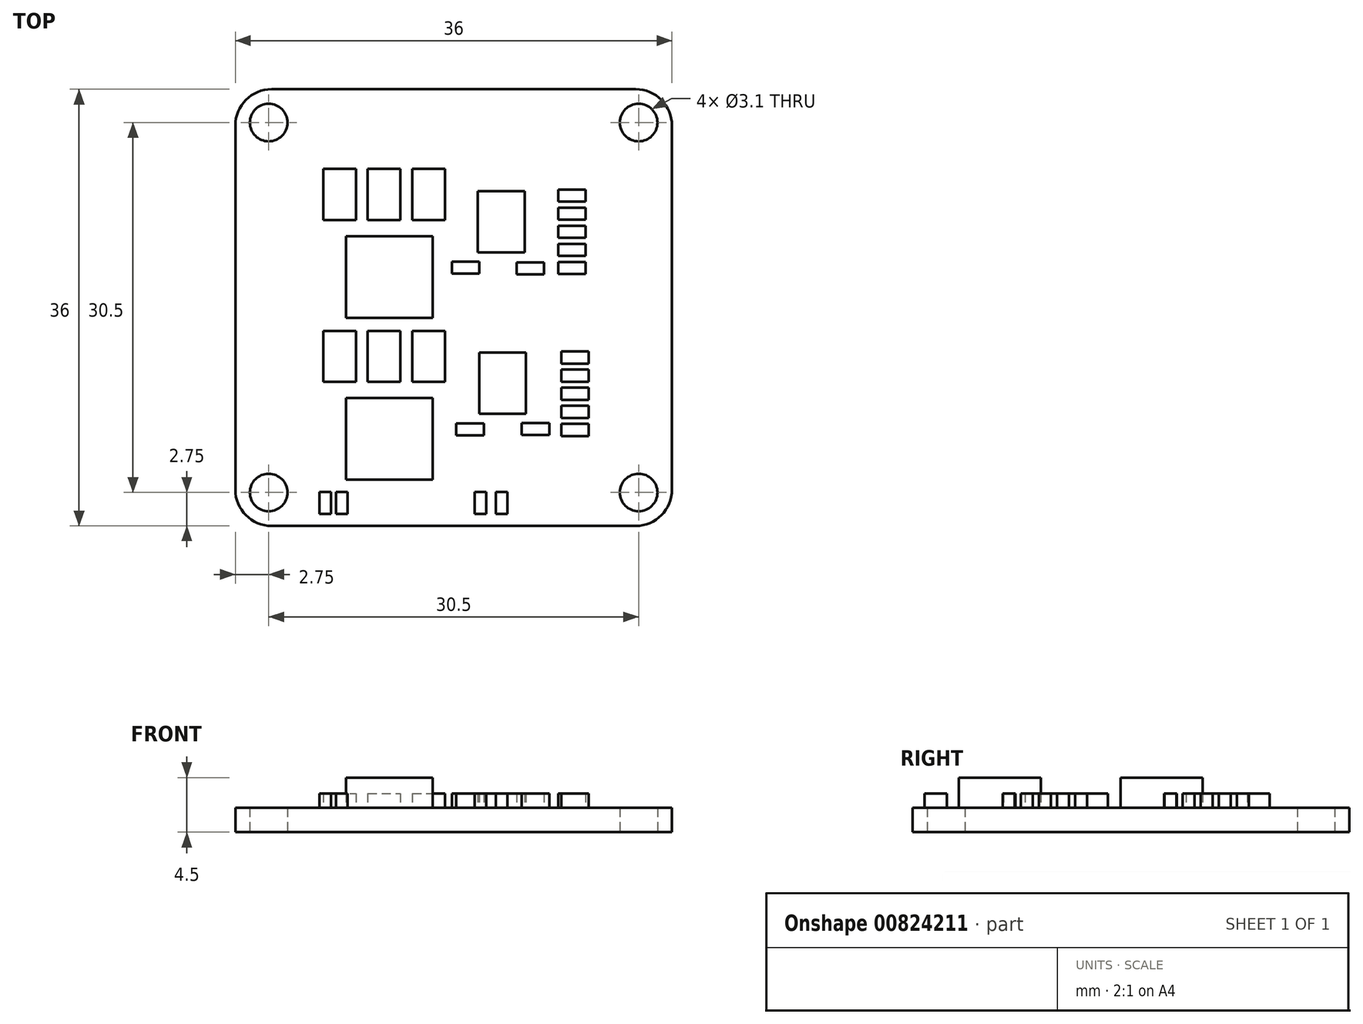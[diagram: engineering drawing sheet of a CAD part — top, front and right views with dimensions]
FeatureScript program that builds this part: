
annotation { "Feature Type Name" : "Feature", "Feature Type Description" : "" }
export const myFeature = defineFeature(function(context is Context, id is Id, definition is map)
    precondition{}
    {
        {
            var Q0;
            Q0=qCreatedBy(makeId("Top.planeOp"),FACE);
            var sketch = newSketch(context, id + "F0", { "sketchPlane" : qUnion([Q0])});
            skLineSegment(sketch, "E0", {"start": v(18, 17.73) * mm, "end": v(-18, -17.73) * mm, "construction": true});
            skLineSegment(sketch, "E1.bottom", {"start": v(18, -18) * mm, "end": v(-18, -18) * mm});
            skLineSegment(sketch, "E1.top", {"start": v(18, 18) * mm, "end": v(-18, 18) * mm});
            skLineSegment(sketch, "E1.left", {"start": v(18, -18) * mm, "end": v(18, 18) * mm});
            skLineSegment(sketch, "E1.right", {"start": v(-18, -18) * mm, "end": v(-18, 18) * mm});
            skPoint(sketch, "E1.middle", {"position": v(0, 0) * mm});
            skLineSegment(sketch, "E2.bottom", {"start": v(15.25, -15.25) * mm, "end": v(-15.25, -15.25) * mm, "construction": true});
            skLineSegment(sketch, "E2.top", {"start": v(15.25, 15.25) * mm, "end": v(-15.25, 15.25) * mm, "construction": true});
            skLineSegment(sketch, "E2.left", {"start": v(15.25, -15.25) * mm, "end": v(15.25, 15.25) * mm, "construction": true});
            skLineSegment(sketch, "E2.right", {"start": v(-15.25, -15.25) * mm, "end": v(-15.25, 15.25) * mm, "construction": true});
            skCircle(sketch, "E3", {"center": v(-15.25, 15.25) * mm, "radius": 1.55 * mm});
            skCircle(sketch, "E4", {"center": v(15.25, 15.25) * mm, "radius": 1.55 * mm});
            skCircle(sketch, "E5", {"center": v(-15.25, -15.25) * mm, "radius": 1.55 * mm});
            skCircle(sketch, "E6", {"center": v(15.25, -15.25) * mm, "radius": 1.55 * mm});
            skSolve(sketch);
        }
        {
            var Q0;
            Q0 = qSketchRegion(id + "F0", true);
            extrude(context, id + "F1", {"entities" : qUnion([Q0]), "depth" : 2 * mm, "offsetDistance" : 25 * mm});
        }
        {
            var Q0;
            Q0=makeQuery(id+"F1.opExtrude","CAP_FACE",FACE,{"disambiguationData":[OSD([sQuery(id+"F0.wireOp",EDGE,"E1.bottom"),sQuery(id+"F0.wireOp",EDGE,"E1.top"),sQuery(id+"F0.wireOp",EDGE,"E1.left"),sQuery(id+"F0.wireOp",EDGE,"E1.right"),sQuery(id+"F0.wireOp",EDGE,"E3"),sQuery(id+"F0.wireOp",EDGE,"E4"),sQuery(id+"F0.wireOp",EDGE,"E5"),sQuery(id+"F0.wireOp",EDGE,"E6")])],"isStart":false});
            var sketch = newSketch(context, id + "F2", { "sketchPlane" : qUnion([Q0])});
            skLineSegment(sketch, "E7.bottom", {"start": v(-10.76, 11.42) * mm, "end": v(-8.06, 11.42) * mm});
            skLineSegment(sketch, "E7.top", {"start": v(-10.76, 7.22) * mm, "end": v(-8.06, 7.22) * mm});
            skLineSegment(sketch, "E7.left", {"start": v(-10.76, 11.42) * mm, "end": v(-10.76, 7.22) * mm});
            skLineSegment(sketch, "E7.right", {"start": v(-8.06, 11.42) * mm, "end": v(-8.06, 7.22) * mm});
            skLineSegment(sketch, "E8.0.1.0", {"start": v(-10.76, -1.92) * mm, "end": v(-8.06, -1.92) * mm});
            skLineSegment(sketch, "E8.0.1.1", {"start": v(-10.76, -1.92) * mm, "end": v(-10.76, -6.12) * mm});
            skLineSegment(sketch, "E8.0.1.2", {"start": v(-8.06, -1.92) * mm, "end": v(-8.06, -6.12) * mm});
            skLineSegment(sketch, "E8.0.1.3", {"start": v(-10.76, -6.12) * mm, "end": v(-8.06, -6.12) * mm});
            skLineSegment(sketch, "E8.1.0.0", {"start": v(-7.08, 11.42) * mm, "end": v(-4.38, 11.42) * mm});
            skLineSegment(sketch, "E8.1.0.1", {"start": v(-7.08, 11.42) * mm, "end": v(-7.08, 7.22) * mm});
            skLineSegment(sketch, "E8.1.0.2", {"start": v(-4.38, 11.42) * mm, "end": v(-4.38, 7.22) * mm});
            skLineSegment(sketch, "E8.1.0.3", {"start": v(-7.08, 7.22) * mm, "end": v(-4.38, 7.22) * mm});
            skLineSegment(sketch, "E8.1.1.0", {"start": v(-7.08, -1.92) * mm, "end": v(-4.38, -1.92) * mm});
            skLineSegment(sketch, "E8.1.1.1", {"start": v(-7.08, -1.92) * mm, "end": v(-7.08, -6.12) * mm});
            skLineSegment(sketch, "E8.1.1.2", {"start": v(-4.38, -1.92) * mm, "end": v(-4.38, -6.12) * mm});
            skLineSegment(sketch, "E8.1.1.3", {"start": v(-7.08, -6.12) * mm, "end": v(-4.38, -6.12) * mm});
            skLineSegment(sketch, "E8.2.0.0", {"start": v(-3.41, 11.42) * mm, "end": v(-0.71, 11.42) * mm});
            skLineSegment(sketch, "E8.2.0.1", {"start": v(-3.41, 11.42) * mm, "end": v(-3.41, 7.22) * mm});
            skLineSegment(sketch, "E8.2.0.2", {"start": v(-0.71, 11.42) * mm, "end": v(-0.71, 7.22) * mm});
            skLineSegment(sketch, "E8.2.0.3", {"start": v(-3.41, 7.22) * mm, "end": v(-0.71, 7.22) * mm});
            skLineSegment(sketch, "E8.2.1.0", {"start": v(-3.41, -1.92) * mm, "end": v(-0.71, -1.92) * mm});
            skLineSegment(sketch, "E8.2.1.1", {"start": v(-3.41, -1.92) * mm, "end": v(-3.41, -6.12) * mm});
            skLineSegment(sketch, "E8.2.1.2", {"start": v(-0.71, -1.92) * mm, "end": v(-0.71, -6.12) * mm});
            skLineSegment(sketch, "E8.2.1.3", {"start": v(-3.41, -6.12) * mm, "end": v(-0.71, -6.12) * mm});
            skLineSegment(sketch, "E8.direction1", {"start": v(-10.76, 7.22) * mm, "end": v(-7.08, 7.22) * mm, "construction": true});
            skLineSegment(sketch, "E8.direction2", {"start": v(-10.76, 7.22) * mm, "end": v(-10.76, -6.12) * mm, "construction": true});
            skLineSegment(sketch, "E9.bottom", {"start": v(1.98, 9.58) * mm, "end": v(5.84, 9.58) * mm});
            skLineSegment(sketch, "E9.top", {"start": v(1.98, 4.53) * mm, "end": v(5.84, 4.53) * mm});
            skLineSegment(sketch, "E9.left", {"start": v(1.98, 9.58) * mm, "end": v(1.98, 4.53) * mm});
            skLineSegment(sketch, "E9.right", {"start": v(5.84, 9.58) * mm, "end": v(5.84, 4.53) * mm});
            skLineSegment(sketch, "E10.bottom", {"start": v(2.1, -3.7) * mm, "end": v(5.97, -3.7) * mm});
            skLineSegment(sketch, "E10.top", {"start": v(2.1, -8.75) * mm, "end": v(5.97, -8.75) * mm});
            skLineSegment(sketch, "E10.left", {"start": v(2.1, -3.7) * mm, "end": v(2.1, -8.75) * mm});
            skLineSegment(sketch, "E10.right", {"start": v(5.97, -3.7) * mm, "end": v(5.97, -8.75) * mm});
            skLineSegment(sketch, "E11.bottom", {"start": v(8.62, 9.72) * mm, "end": v(10.88, 9.72) * mm});
            skLineSegment(sketch, "E11.top", {"start": v(8.62, 8.73) * mm, "end": v(10.88, 8.73) * mm});
            skLineSegment(sketch, "E11.left", {"start": v(8.62, 9.72) * mm, "end": v(8.62, 8.73) * mm});
            skLineSegment(sketch, "E11.right", {"start": v(10.88, 9.72) * mm, "end": v(10.88, 8.73) * mm});
            skLineSegment(sketch, "E12.1.0.0", {"start": v(10.88, 8.23) * mm, "end": v(10.88, 7.24) * mm});
            skLineSegment(sketch, "E12.1.0.1", {"start": v(8.62, 8.23) * mm, "end": v(8.62, 7.24) * mm});
            skLineSegment(sketch, "E12.1.0.2", {"start": v(8.62, 8.23) * mm, "end": v(10.88, 8.23) * mm});
            skLineSegment(sketch, "E12.1.0.3", {"start": v(8.62, 7.24) * mm, "end": v(10.88, 7.24) * mm});
            skLineSegment(sketch, "E12.2.0.0", {"start": v(10.88, 6.73) * mm, "end": v(10.88, 5.74) * mm});
            skLineSegment(sketch, "E12.2.0.1", {"start": v(8.62, 6.73) * mm, "end": v(8.62, 5.74) * mm});
            skLineSegment(sketch, "E12.2.0.2", {"start": v(8.62, 6.73) * mm, "end": v(10.88, 6.73) * mm});
            skLineSegment(sketch, "E12.2.0.3", {"start": v(8.62, 5.74) * mm, "end": v(10.88, 5.74) * mm});
            skLineSegment(sketch, "E12.3.0.0", {"start": v(10.88, 5.24) * mm, "end": v(10.88, 4.25) * mm});
            skLineSegment(sketch, "E12.3.0.1", {"start": v(8.62, 5.24) * mm, "end": v(8.62, 4.25) * mm});
            skLineSegment(sketch, "E12.3.0.2", {"start": v(8.62, 5.24) * mm, "end": v(10.88, 5.24) * mm});
            skLineSegment(sketch, "E12.3.0.3", {"start": v(8.62, 4.25) * mm, "end": v(10.88, 4.25) * mm});
            skLineSegment(sketch, "E12.4.0.0", {"start": v(10.88, 3.75) * mm, "end": v(10.88, 2.76) * mm});
            skLineSegment(sketch, "E12.4.0.1", {"start": v(8.62, 3.75) * mm, "end": v(8.62, 2.76) * mm});
            skLineSegment(sketch, "E12.4.0.2", {"start": v(8.62, 3.75) * mm, "end": v(10.88, 3.75) * mm});
            skLineSegment(sketch, "E12.4.0.3", {"start": v(8.62, 2.76) * mm, "end": v(10.88, 2.76) * mm});
            skLineSegment(sketch, "E12.direction1", {"start": v(8.62, 8.73) * mm, "end": v(8.62, 7.24) * mm, "construction": true});
            skLineSegment(sketch, "E13.bottom", {"start": v(8.86, -3.63) * mm, "end": v(11.13, -3.63) * mm});
            skLineSegment(sketch, "E13.top", {"start": v(8.86, -4.62) * mm, "end": v(11.13, -4.62) * mm});
            skLineSegment(sketch, "E13.left", {"start": v(8.86, -3.63) * mm, "end": v(8.86, -4.62) * mm});
            skLineSegment(sketch, "E13.right", {"start": v(11.13, -3.63) * mm, "end": v(11.13, -4.62) * mm});
            skLineSegment(sketch, "E14.1.0.0", {"start": v(11.13, -5.12) * mm, "end": v(11.13, -6.1) * mm});
            skLineSegment(sketch, "E14.1.0.1", {"start": v(8.86, -5.12) * mm, "end": v(8.86, -6.1) * mm});
            skLineSegment(sketch, "E14.1.0.2", {"start": v(8.86, -5.12) * mm, "end": v(11.13, -5.12) * mm});
            skLineSegment(sketch, "E14.1.0.3", {"start": v(8.86, -6.1) * mm, "end": v(11.13, -6.1) * mm});
            skLineSegment(sketch, "E14.2.0.0", {"start": v(11.13, -6.61) * mm, "end": v(11.13, -7.6) * mm});
            skLineSegment(sketch, "E14.2.0.1", {"start": v(8.86, -6.61) * mm, "end": v(8.86, -7.6) * mm});
            skLineSegment(sketch, "E14.2.0.2", {"start": v(8.86, -6.61) * mm, "end": v(11.13, -6.61) * mm});
            skLineSegment(sketch, "E14.2.0.3", {"start": v(8.86, -7.6) * mm, "end": v(11.13, -7.6) * mm});
            skLineSegment(sketch, "E14.3.0.0", {"start": v(11.13, -8.1) * mm, "end": v(11.13, -9.1) * mm});
            skLineSegment(sketch, "E14.3.0.1", {"start": v(8.86, -8.1) * mm, "end": v(8.86, -9.1) * mm});
            skLineSegment(sketch, "E14.3.0.2", {"start": v(8.86, -8.1) * mm, "end": v(11.13, -8.1) * mm});
            skLineSegment(sketch, "E14.3.0.3", {"start": v(8.86, -9.1) * mm, "end": v(11.13, -9.1) * mm});
            skLineSegment(sketch, "E14.4.0.0", {"start": v(11.13, -9.6) * mm, "end": v(11.13, -10.59) * mm});
            skLineSegment(sketch, "E14.4.0.1", {"start": v(8.86, -9.6) * mm, "end": v(8.86, -10.59) * mm});
            skLineSegment(sketch, "E14.4.0.2", {"start": v(8.86, -9.6) * mm, "end": v(11.13, -9.6) * mm});
            skLineSegment(sketch, "E14.4.0.3", {"start": v(8.86, -10.59) * mm, "end": v(11.13, -10.59) * mm});
            skLineSegment(sketch, "E14.direction1", {"start": v(8.86, -4.62) * mm, "end": v(8.86, -6.1) * mm, "construction": true});
            skLineSegment(sketch, "E15.bottom", {"start": v(-0.15, 3.79) * mm, "end": v(2.12, 3.79) * mm});
            skLineSegment(sketch, "E15.top", {"start": v(-0.15, 2.8) * mm, "end": v(2.12, 2.8) * mm});
            skLineSegment(sketch, "E15.left", {"start": v(-0.15, 3.79) * mm, "end": v(-0.15, 2.8) * mm});
            skLineSegment(sketch, "E15.right", {"start": v(2.12, 3.79) * mm, "end": v(2.12, 2.8) * mm});
            skLineSegment(sketch, "E16.bottom", {"start": v(5.19, 3.72) * mm, "end": v(7.45, 3.72) * mm});
            skLineSegment(sketch, "E16.top", {"start": v(5.19, 2.73) * mm, "end": v(7.45, 2.73) * mm});
            skLineSegment(sketch, "E16.left", {"start": v(5.19, 3.72) * mm, "end": v(5.19, 2.73) * mm});
            skLineSegment(sketch, "E16.right", {"start": v(7.45, 3.72) * mm, "end": v(7.45, 2.73) * mm});
            skLineSegment(sketch, "E17.bottom", {"start": v(0.22, -9.55) * mm, "end": v(2.48, -9.55) * mm});
            skLineSegment(sketch, "E17.top", {"start": v(0.22, -10.54) * mm, "end": v(2.48, -10.54) * mm});
            skLineSegment(sketch, "E17.left", {"start": v(0.22, -9.55) * mm, "end": v(0.22, -10.54) * mm});
            skLineSegment(sketch, "E17.right", {"start": v(2.48, -9.55) * mm, "end": v(2.48, -10.54) * mm});
            skLineSegment(sketch, "E18.bottom", {"start": v(5.62, -9.52) * mm, "end": v(7.88, -9.52) * mm});
            skLineSegment(sketch, "E18.top", {"start": v(5.62, -10.5) * mm, "end": v(7.88, -10.5) * mm});
            skLineSegment(sketch, "E18.left", {"start": v(5.62, -9.52) * mm, "end": v(5.62, -10.5) * mm});
            skLineSegment(sketch, "E18.right", {"start": v(7.88, -9.52) * mm, "end": v(7.88, -10.5) * mm});
            skLineSegment(sketch, "E19.bottom", {"start": v(-11.06, -15.2) * mm, "end": v(-10.1, -15.2) * mm});
            skLineSegment(sketch, "E19.top", {"start": v(-11.06, -17.02) * mm, "end": v(-10.1, -17.02) * mm});
            skLineSegment(sketch, "E19.left", {"start": v(-11.06, -15.2) * mm, "end": v(-11.06, -17.02) * mm});
            skLineSegment(sketch, "E19.right", {"start": v(-10.1, -15.2) * mm, "end": v(-10.1, -17.02) * mm});
            skLineSegment(sketch, "E20.bottom", {"start": v(-9.7, -15.2) * mm, "end": v(-8.75, -15.2) * mm});
            skLineSegment(sketch, "E20.top", {"start": v(-9.7, -17.02) * mm, "end": v(-8.75, -17.02) * mm});
            skLineSegment(sketch, "E20.left", {"start": v(-9.7, -15.2) * mm, "end": v(-9.7, -17.02) * mm});
            skLineSegment(sketch, "E20.right", {"start": v(-8.75, -15.2) * mm, "end": v(-8.75, -17.02) * mm});
            skLineSegment(sketch, "E21.bottom", {"start": v(1.73, -15.2) * mm, "end": v(2.68, -15.2) * mm});
            skLineSegment(sketch, "E21.top", {"start": v(1.73, -17.02) * mm, "end": v(2.68, -17.02) * mm});
            skLineSegment(sketch, "E21.left", {"start": v(1.73, -15.2) * mm, "end": v(1.73, -17.02) * mm});
            skLineSegment(sketch, "E21.right", {"start": v(2.68, -15.2) * mm, "end": v(2.68, -17.02) * mm});
            skLineSegment(sketch, "E22.bottom", {"start": v(3.5, -15.2) * mm, "end": v(4.44, -15.2) * mm});
            skLineSegment(sketch, "E22.top", {"start": v(3.5, -17.02) * mm, "end": v(4.44, -17.02) * mm});
            skLineSegment(sketch, "E22.left", {"start": v(3.5, -15.2) * mm, "end": v(3.5, -17.02) * mm});
            skLineSegment(sketch, "E22.right", {"start": v(4.44, -15.2) * mm, "end": v(4.44, -17.02) * mm});
            skSolve(sketch);
        }
        {
            var Q0;
            Q0 = qSketchRegion(id + "F2", true);
            extrude(context, id + "F3", {"entities" : qUnion([Q0]), "operationType" : NewBodyOperationType.ADD, "depth" : 1.2 * mm, "offsetDistance" : 25 * mm});
        }
        {
            var Q0;
            Q0=makeQuery(id+"F1.opExtrude","CAP_FACE",FACE,{"disambiguationData":[OSD([sQuery(id+"F0.wireOp",EDGE,"E1.bottom"),sQuery(id+"F0.wireOp",EDGE,"E1.top"),sQuery(id+"F0.wireOp",EDGE,"E1.left"),sQuery(id+"F0.wireOp",EDGE,"E1.right"),sQuery(id+"F0.wireOp",EDGE,"E3"),sQuery(id+"F0.wireOp",EDGE,"E4"),sQuery(id+"F0.wireOp",EDGE,"E5"),sQuery(id+"F0.wireOp",EDGE,"E6")])],"isStart":false});
            var sketch = newSketch(context, id + "F4", { "sketchPlane" : qUnion([Q0])});
            skLineSegment(sketch, "E23.bottom", {"start": v(-8.87, 5.89) * mm, "end": v(-1.72, 5.89) * mm});
            skLineSegment(sketch, "E23.top", {"start": v(-8.87, -0.86) * mm, "end": v(-1.72, -0.86) * mm});
            skLineSegment(sketch, "E23.left", {"start": v(-8.87, 5.89) * mm, "end": v(-8.87, -0.86) * mm});
            skLineSegment(sketch, "E23.right", {"start": v(-1.72, 5.89) * mm, "end": v(-1.72, -0.86) * mm});
            skLineSegment(sketch, "E24.bottom", {"start": v(-8.87, -7.45) * mm, "end": v(-1.72, -7.45) * mm});
            skLineSegment(sketch, "E24.top", {"start": v(-8.87, -14.19) * mm, "end": v(-1.72, -14.19) * mm});
            skLineSegment(sketch, "E24.left", {"start": v(-8.87, -7.45) * mm, "end": v(-8.87, -14.19) * mm});
            skLineSegment(sketch, "E24.right", {"start": v(-1.72, -7.45) * mm, "end": v(-1.72, -14.19) * mm});
            skSolve(sketch);
        }
        {
            var Q0;
            Q0 = qSketchRegion(id + "F4", true);
            extrude(context, id + "F5", {"entities" : qUnion([Q0]), "operationType" : NewBodyOperationType.ADD, "depth" : 2.5 * mm, "offsetDistance" : 25 * mm});
        }
        {
            var Q0;
            Q0=makeQuery(id+"F1.opExtrude","SWEPT_EDGE",EDGE,{"disambiguationData":[OSD([sQuery(id+"F0.wireOp",EDGE,"E1.top"),sQuery(id+"F0.wireOp",EDGE,"E1.right")])]});
            var Q1;
            Q1=makeQuery(id+"F1.opExtrude","SWEPT_EDGE",EDGE,{"disambiguationData":[OSD([sQuery(id+"F0.wireOp",EDGE,"E1.bottom"),sQuery(id+"F0.wireOp",EDGE,"E1.right")])]});
            var Q2;
            Q2=makeQuery(id+"F1.opExtrude","SWEPT_EDGE",EDGE,{"disambiguationData":[OSD([sQuery(id+"F0.wireOp",EDGE,"E1.bottom"),sQuery(id+"F0.wireOp",EDGE,"E1.left")])]});
            var Q3;
            Q3=makeQuery(id+"F1.opExtrude","SWEPT_EDGE",EDGE,{"disambiguationData":[OSD([sQuery(id+"F0.wireOp",EDGE,"E1.top"),sQuery(id+"F0.wireOp",EDGE,"E1.left")])]});
            fillet(context, id + "F6", {"entities" : qUnion([Q0, Q1, Q2, Q3]), "radius" : 3 * mm, "tangentPropagation" : true, "allowEdgeOverflow" : false});
        }
    });
